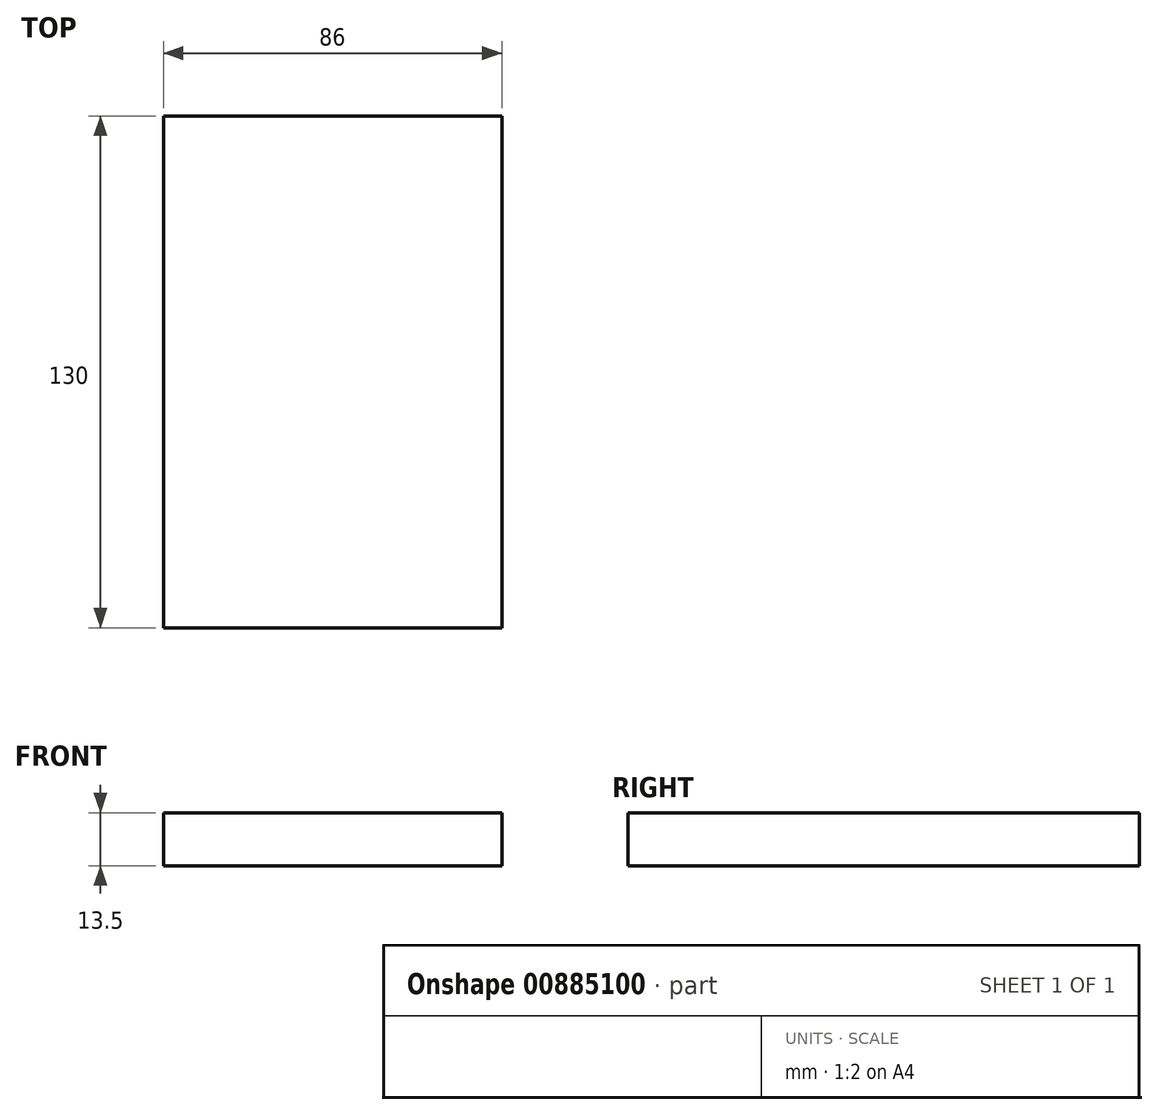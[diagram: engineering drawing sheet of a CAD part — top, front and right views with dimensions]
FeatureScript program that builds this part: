
annotation { "Feature Type Name" : "Feature", "Feature Type Description" : "" }
export const myFeature = defineFeature(function(context is Context, id is Id, definition is map)
    precondition{}
    {
        {
            var Q0;
            Q0=qCreatedBy(makeId("Top.planeOp"),FACE);
            var sketch = newSketch(context, id + "F0", { "sketchPlane" : qUnion([Q0])});
            skLineSegment(sketch, "E0.bottom", {"start": v(-48.27, 70.29) * mm, "end": v(37.73, 70.29) * mm});
            skLineSegment(sketch, "E0.top", {"start": v(-48.27, -59.71) * mm, "end": v(37.73, -59.71) * mm});
            skLineSegment(sketch, "E0.left", {"start": v(-48.27, 70.29) * mm, "end": v(-48.27, -59.71) * mm});
            skLineSegment(sketch, "E0.right", {"start": v(37.73, 70.29) * mm, "end": v(37.73, -59.71) * mm});
            skSolve(sketch);
        }
        {
            var Q0;
            Q0=makeQuery(id+"F0.imprint","IMPRINT",FACE,{"disambiguationData":[TD([[makeQuery(id+"F0.imprint","IMPRINT",EDGE,{"derivedFrom":sQuery(id+"F0.wireOp",EDGE,"E0.bottom")}),-1.0]])]});
            extrude(context, id + "F1", {"entities" : qUnion([Q0]), "depth" : 13.5 * mm, "offsetDistance" : 25.4 * mm});
        }
    });
